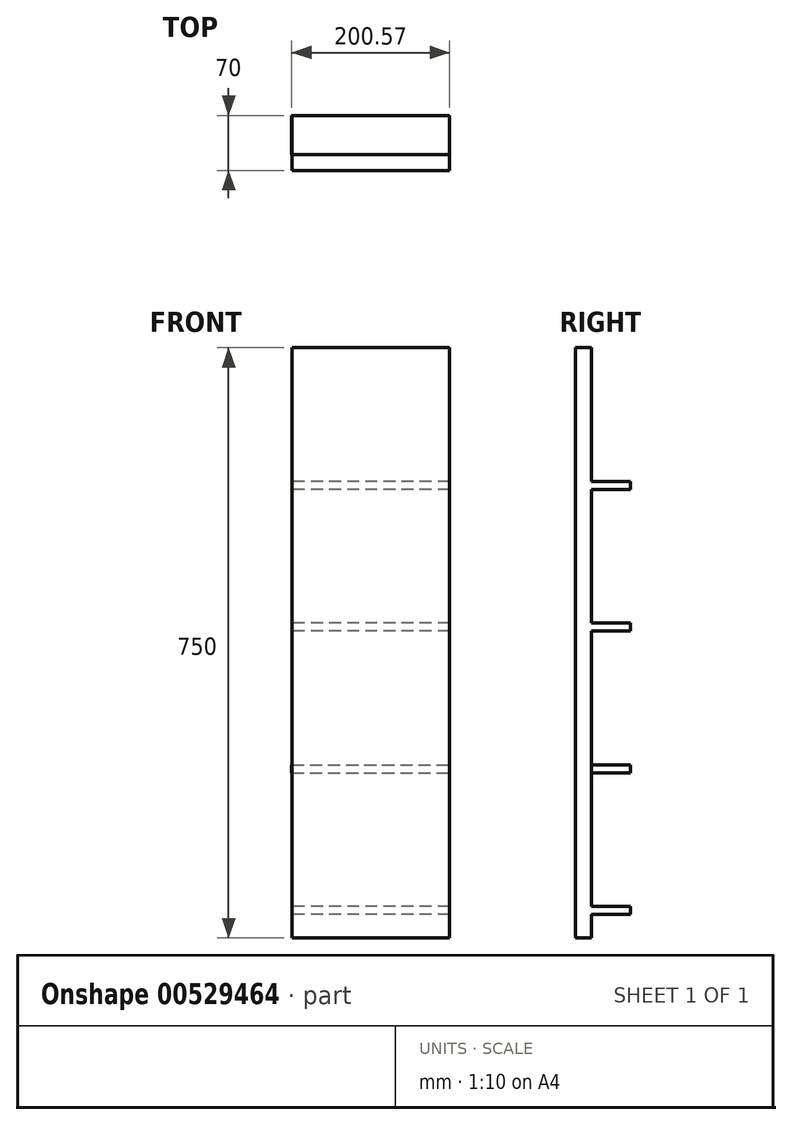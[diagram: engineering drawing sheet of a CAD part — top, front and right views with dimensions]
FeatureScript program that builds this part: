
annotation { "Feature Type Name" : "Feature", "Feature Type Description" : "" }
export const myFeature = defineFeature(function(context is Context, id is Id, definition is map)
    precondition{}
    {
        {
            var Q0;
            Q0=qCreatedBy(makeId("Front.planeOp"),FACE);
            var sketch = newSketch(context, id + "F0", { "sketchPlane" : qUnion([Q0])});
            skLineSegment(sketch, "E0.bottom", {"start": v(-317.5, 434.85) * mm, "end": v(-117.5, 434.85) * mm});
            skLineSegment(sketch, "E0.top", {"start": v(-317.5, -315.15) * mm, "end": v(-117.5, -315.15) * mm});
            skLineSegment(sketch, "E0.left", {"start": v(-317.5, 434.85) * mm, "end": v(-317.5, -315.15) * mm});
            skLineSegment(sketch, "E0.right", {"start": v(-117.5, 434.85) * mm, "end": v(-117.5, -315.15) * mm});
            skSolve(sketch);
        }
        {
            var Q0;
            Q0=makeQuery(id+"F0.imprint","IMPRINT",FACE,{"disambiguationData":[TD([[makeQuery(id+"F0.imprint","IMPRINT",EDGE,{"derivedFrom":sQuery(id+"F0.wireOp",EDGE,"E0.bottom")}),-1.0]])]});
            extrude(context, id + "F1", {"entities" : qUnion([Q0]), "depth" : 20 * mm, "offsetDistance" : 25.4 * mm});
        }
        {
            var Q0;
            Q0=qCreatedBy(makeId("Front.planeOp"),FACE);
            var sketch = newSketch(context, id + "F2", { "sketchPlane" : qUnion([Q0])});
            skLineSegment(sketch, "E1.bottom", {"start": v(-318.07, -105.15) * mm, "end": v(-118.07, -105.15) * mm});
            skLineSegment(sketch, "E1.top", {"start": v(-318.07, -95.15) * mm, "end": v(-118.07, -95.15) * mm});
            skLineSegment(sketch, "E1.left", {"start": v(-318.07, -105.15) * mm, "end": v(-318.07, -95.15) * mm});
            skLineSegment(sketch, "E1.right", {"start": v(-118.07, -105.15) * mm, "end": v(-118.07, -95.15) * mm});
            skPoint(sketch, "E1.middle", {"position": v(-218.07, -100.15) * mm});
            skSolve(sketch);
        }
        {
            var Q0;
            Q0=makeQuery(id+"F2.imprint","IMPRINT",FACE,{"disambiguationData":[TD([[makeQuery(id+"F2.imprint","IMPRINT",EDGE,{"derivedFrom":sQuery(id+"F2.wireOp",EDGE,"E1.bottom")}),1.0]])]});
            extrude(context, id + "F3", {"entities" : qUnion([Q0]), "operationType" : NewBodyOperationType.ADD, "oppositeDirection" : true, "depth" : 50 * mm, "offsetDistance" : 25.4 * mm});
        }
        {
            var Q0;
            Q0=qCreatedBy(makeId("Front.planeOp"),FACE);
            var sketch = newSketch(context, id + "F4", { "sketchPlane" : qUnion([Q0])});
            skLineSegment(sketch, "E2.bottom", {"start": v(-117.5, 84.85) * mm, "end": v(-317.5, 84.85) * mm});
            skLineSegment(sketch, "E2.top", {"start": v(-117.5, 74.85) * mm, "end": v(-317.5, 74.85) * mm});
            skLineSegment(sketch, "E2.left", {"start": v(-117.5, 84.85) * mm, "end": v(-117.5, 74.85) * mm});
            skLineSegment(sketch, "E2.right", {"start": v(-317.5, 84.85) * mm, "end": v(-317.5, 74.85) * mm});
            skSolve(sketch);
        }
        {
            var Q0;
            Q0=qSketchRegion(id+"F4",true);
            extrude(context, id + "F5", {"entities" : qUnion([Q0]), "operationType" : NewBodyOperationType.ADD, "oppositeDirection" : true, "depth" : 50 * mm, "offsetDistance" : 25.4 * mm});
        }
        {
            var Q0;
            Q0=qCreatedBy(makeId("Front.planeOp"),FACE);
            var sketch = newSketch(context, id + "F6", { "sketchPlane" : qUnion([Q0])});
            skLineSegment(sketch, "E3.bottom", {"start": v(-117.5, 264.85) * mm, "end": v(-317.5, 264.85) * mm});
            skLineSegment(sketch, "E3.top", {"start": v(-117.5, 254.85) * mm, "end": v(-317.5, 254.85) * mm});
            skLineSegment(sketch, "E3.left", {"start": v(-117.5, 264.85) * mm, "end": v(-117.5, 254.85) * mm});
            skLineSegment(sketch, "E3.right", {"start": v(-317.5, 264.85) * mm, "end": v(-317.5, 254.85) * mm});
            skSolve(sketch);
        }
        {
            var Q0;
            Q0=qSketchRegion(id+"F6",true);
            extrude(context, id + "F7", {"entities" : qUnion([Q0]), "operationType" : NewBodyOperationType.ADD, "oppositeDirection" : true, "depth" : 50 * mm, "offsetDistance" : 25.4 * mm});
        }
        {
            var Q0;
            Q0=qCreatedBy(makeId("Front.planeOp"),FACE);
            var sketch = newSketch(context, id + "F8", { "sketchPlane" : qUnion([Q0])});
            skLineSegment(sketch, "E4.bottom", {"start": v(-117.5, -275.15) * mm, "end": v(-317.5, -275.15) * mm});
            skLineSegment(sketch, "E4.top", {"start": v(-117.5, -285.15) * mm, "end": v(-317.5, -285.15) * mm});
            skLineSegment(sketch, "E4.left", {"start": v(-117.5, -275.15) * mm, "end": v(-117.5, -285.15) * mm});
            skLineSegment(sketch, "E4.right", {"start": v(-317.5, -275.15) * mm, "end": v(-317.5, -285.15) * mm});
            skSolve(sketch);
        }
        {
            var Q0;
            Q0=qSketchRegion(id+"F8",true);
            extrude(context, id + "F9", {"entities" : qUnion([Q0]), "operationType" : NewBodyOperationType.ADD, "oppositeDirection" : true, "depth" : 50 * mm, "offsetDistance" : 25.4 * mm});
        }
    });
